# Revit family: UNO-G
name_source: partatom
category: Wyposażenie mechaniczne
revit_build: Autodesk Revit 2017 (Build: 20160225_1515(x64)
units: mm (PartAtom-declared; Revit-internal decimal feet)

## family parameters
Oparty na płaszczyźnie roboczej = Nie
Punkt obliczania pomieszczeń = Nie
Tnij formami wycięć po wczytaniu = Nie
Typ części = Normalny
Współdzielony = Nie
Wymiar okrągłego złącza = Użyj średnicy
Zawsze pionowo = Tak

## types (12) — shared parameters
Date = 09.2018
Frequency = 50 Hz
Producent = Rosenberg
Protection_class = IP54
URL = https://www.rosenberg.pl
Version = 1

## per-type parameters (varying)
| type | A_ABH | A_ELS | A_JKL | A_WSD | Air_flow | B_ABH | B_ELS | B_GR | B_JKL | B_WSD | C_ELS | Current | Diameter | H_FUS | Height | L_FUS | Logo_scale | Model | Power | Pressure | Voltage | Weight[kg] | Width | max.Ambient_temperature |
| 50-315-G.3DI | 300 mm  [stored 0.984252 ft] | 409 mm  [stored 1.34186 ft] | 339 mm  [stored 1.1122 ft] | 600 mm | 1773.0 m³/h | 450 mm  [stored 1.47638 ft] | 433 mm | 464 mm  [stored 1.52231 ft] | 363 mm | 720 mm  [stored 2.3622 ft] | 20 mm  [stored 0.0656168 ft] | 1 A | 203 mm  [stored 0.66601 ft] | 32 mm  [stored 0.104987 ft] | 500 mm  [stored 1.64042 ft] | 600 mm | 1 mm  [stored 0.00328084 ft] | 50-315-G.3DI | 0 kW | 280.0 Pa | 230 V | 30 | 500 mm  [stored 1.64042 ft] | 50 °C |
| 50-315-G.4EA | 300 mm  [stored 0.984252 ft] | 409 mm  [stored 1.34186 ft] | 339 mm  [stored 1.1122 ft] | 600 mm | 2219.0 m³/h | 450 mm  [stored 1.47638 ft] | 433 mm | 464 mm  [stored 1.52231 ft] | 363 mm | 720 mm  [stored 2.3622 ft] | 20 mm  [stored 0.0656168 ft] | 2 A | 203 mm  [stored 0.66601 ft] | 32 mm  [stored 0.104987 ft] | 500 mm  [stored 1.64042 ft] | 600 mm | 1 mm  [stored 0.00328084 ft] | 50-315-G.4EA | 0 kW | 417.0 Pa | 230 V | 31 | 500 mm  [stored 1.64042 ft] | 40 °C |
| 50-355-G.4EA | 300 mm  [stored 0.984252 ft] | 409 mm  [stored 1.34186 ft] | 339 mm  [stored 1.1122 ft] | 600 mm | 2339.0 m³/h | 450 mm  [stored 1.47638 ft] | 433 mm | 464 mm  [stored 1.52231 ft] | 363 mm | 720 mm  [stored 2.3622 ft] | 20 mm  [stored 0.0656168 ft] | 2 A | 228 mm  [stored 0.748031 ft] | 32 mm  [stored 0.104987 ft] | 500 mm  [stored 1.64042 ft] | 600 mm | 1 mm  [stored 0.00328084 ft] | 50-355-G.4EA | 0 kW | 389.0 Pa | 230 V | 33 | 500 mm  [stored 1.64042 ft] | 40 °C |
| 67-400-G.4FF | 380 mm | 579 mm  [stored 1.89961 ft] | 509 mm  [stored 1.66995 ft] | 770 mm  [stored 2.52625 ft] | 3242.0 m³/h | 620 mm  [stored 2.03412 ft] | 633 mm  [stored 2.07677 ft] | 634 mm  [stored 2.08005 ft] | 563 mm  [stored 1.84711 ft] | 800 mm | 20 mm  [stored 0.0656168 ft] | 2 A | 257 mm  [stored 0.843176 ft] | 32 mm  [stored 0.104987 ft] | 620 mm  [stored 2.03412 ft] | 770 mm  [stored 2.52625 ft] | 2 mm  [stored 0.00656168 ft] | 67-400-G.4FF | 0 kW | 291.0 Pa | 230 V | 42.5 | 670 mm  [stored 2.19816 ft] | 40 °C |
| 67-400-G.5FA | 380 mm | 579 mm  [stored 1.89961 ft] | 509 mm  [stored 1.66995 ft] | 770 mm  [stored 2.52625 ft] | 4308.0 m³/h | 620 mm  [stored 2.03412 ft] | 633 mm  [stored 2.07677 ft] | 634 mm  [stored 2.08005 ft] | 563 mm  [stored 1.84711 ft] | 800 mm | 20 mm  [stored 0.0656168 ft] | 5 A | 257 mm  [stored 0.843176 ft] | 32 mm  [stored 0.104987 ft] | 620 mm  [stored 2.03412 ft] | 770 mm  [stored 2.52625 ft] | 2 mm  [stored 0.00656168 ft] | 67-400-G.5FA | 1 kW | 528.0 Pa | 230 V | 55 | 670 mm  [stored 2.19816 ft] | 40 °C |
| 67-450-G.5FA | 380 mm | 579 mm  [stored 1.89961 ft] | 509 mm  [stored 1.66995 ft] | 770 mm  [stored 2.52625 ft] | 4933.0 m³/h | 620 mm  [stored 2.03412 ft] | 633 mm  [stored 2.07677 ft] | 634 mm  [stored 2.08005 ft] | 563 mm  [stored 1.84711 ft] | 800 mm | 20 mm  [stored 0.0656168 ft] | 5 A | 289 mm  [stored 0.948163 ft] | 32 mm  [stored 0.104987 ft] | 620 mm  [stored 2.03412 ft] | 770 mm  [stored 2.52625 ft] | 2 mm  [stored 0.00656168 ft] | 67-450-G.5FA | 1 kW | 445.0 Pa | 230 V | 55 | 670 mm  [stored 2.19816 ft] | 40 °C |
| 80-500-G.5HF | 430 mm | 659 mm  [stored 2.16207 ft] | 589 mm | 900 mm | 5289.0 m³/h | 720 mm  [stored 2.3622 ft] | 697 mm  [stored 2.28675 ft] | 764 mm  [stored 2.50656 ft] | 627 mm  [stored 2.05709 ft] | 890 mm | 30 mm  [stored 0.0984252 ft] | 5 A | 325 mm  [stored 1.06627 ft] | 53 mm | 720 mm  [stored 2.3622 ft] | 900 mm | 2 mm  [stored 0.00656168 ft] | 80-500-G.5HF | 1 kW | 431.0 Pa | 230 V | 84 | 800 mm | 40 °C |
| 102-630-G.6IF | 520 mm  [stored 1.70604 ft] | 879 mm | 809 mm | 1120 mm | 9107.0 m³/h | 940 mm | 917 mm | 984 mm | 847 mm | 1180 mm | 30 mm  [stored 0.0984252 ft] | 4 A | 410 mm  [stored 1.34514 ft] | 53 mm | 940 mm | 1120 mm | 2 mm  [stored 0.00656168 ft] | 102-630-G.6IF | 2 kW | 554.0 Pa | 400 V | 94 | 1020 mm | 50 °C |
| 102-710-G.6NA | 520 mm  [stored 1.70604 ft] | 879 mm | 809 mm | 1120 mm | 12338.0 m³/h | 940 mm | 917 mm | 984 mm | 847 mm | 1180 mm | 30 mm  [stored 0.0984252 ft] | 4 A | 460 mm  [stored 1.50919 ft] | 53 mm | 940 mm | 1120 mm | 2 mm  [stored 0.00656168 ft] | 102-710-G.6NA | 3 kW | 483.0 Pa | 400 V | 100 | 1020 mm | 50 °C |
| 67-450-G.5HF | 380 mm | 579 mm  [stored 1.89961 ft] | 509 mm  [stored 1.66995 ft] | 770 mm  [stored 2.52625 ft] | 5027.0 m³/h | 620 mm  [stored 2.03412 ft] | 633 mm  [stored 2.07677 ft] | 634 mm  [stored 2.08005 ft] | 563 mm  [stored 1.84711 ft] | 800 mm | 20 mm  [stored 0.0656168 ft] | 2 A | 289 mm  [stored 0.948163 ft] | 32 mm  [stored 0.104987 ft] | 620 mm  [stored 2.03412 ft] | 770 mm  [stored 2.52625 ft] | 2 mm  [stored 0.00656168 ft] | 67-450-G.5HF | 1 kW | 586.0 Pa | 400 V | 55 | 670 mm  [stored 2.19816 ft] | 45 °C |
| 80-500-G.6FF | 430 mm | 659 mm  [stored 2.16207 ft] | 589 mm | 900 mm | 7392.0 m³/h | 720 mm  [stored 2.3622 ft] | 697 mm  [stored 2.28675 ft] | 764 mm  [stored 2.50656 ft] | 627 mm  [stored 2.05709 ft] | 890 mm | 30 mm  [stored 0.0984252 ft] | 4 A | 325 mm  [stored 1.06627 ft] | 53 mm | 720 mm  [stored 2.3622 ft] | 900 mm | 2 mm  [stored 0.00656168 ft] | 80-500-G.6FF | 3 kW | 819.0 Pa | 400 V | 84 | 800 mm | 55 °C |
| 80-560-G.6IF | 430 mm | 659 mm  [stored 2.16207 ft] | 589 mm | 900 mm | 9017.0 m³/h | 720 mm  [stored 2.3622 ft] | 697 mm  [stored 2.28675 ft] | 764 mm  [stored 2.50656 ft] | 627 mm  [stored 2.05709 ft] | 1040 mm | 30 mm  [stored 0.0984252 ft] | 5 A | 365 mm  [stored 1.19751 ft] | 53 mm | 800 mm | 900 mm | 2 mm  [stored 0.00656168 ft] | 80-500-G.6FF | 3 kW | 739.0 Pa | 400 V | 85 | 800 mm | 45 °C |

note: [stored X ft] marks values corroborated as IEEE doubles in the binary element streams (Revit-internal decimal feet)
